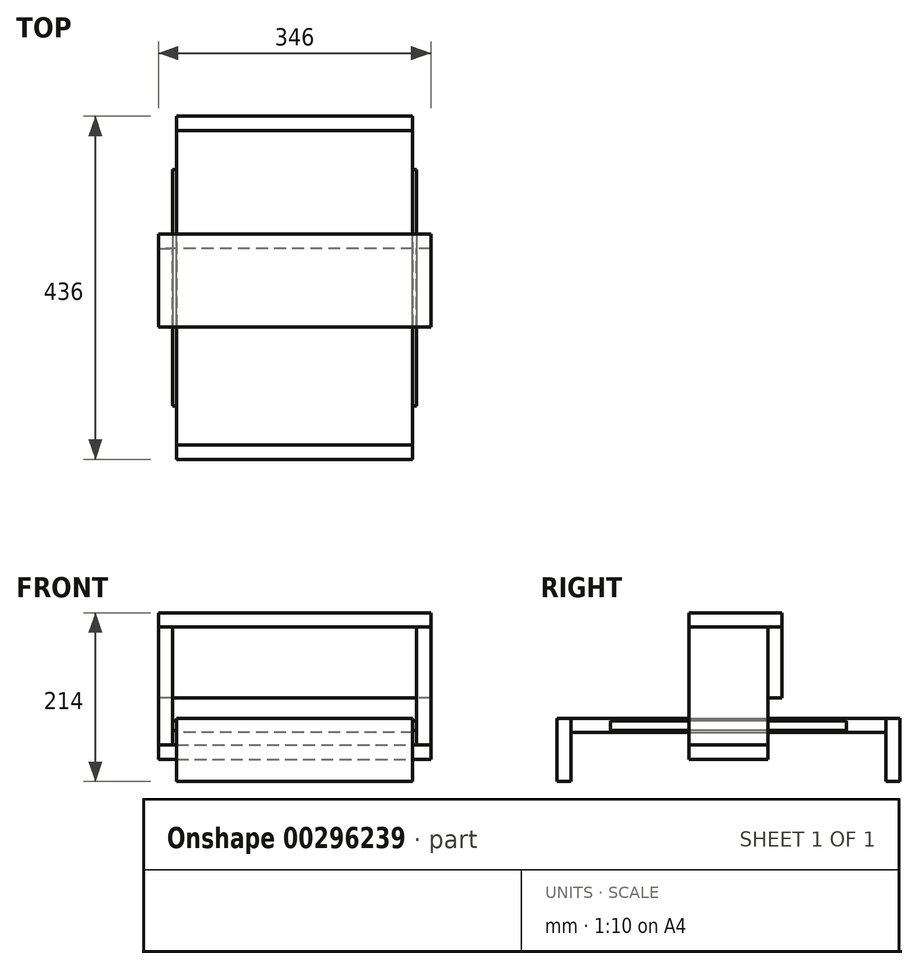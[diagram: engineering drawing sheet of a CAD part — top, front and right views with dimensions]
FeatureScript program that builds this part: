
annotation { "Feature Type Name" : "Feature", "Feature Type Description" : "" }
export const myFeature = defineFeature(function(context is Context, id is Id, definition is map)
    precondition{}
    {
        {
            var Q0;
            Q0=qCreatedBy(makeId("Front.planeOp"),FACE);
            var sketch = newSketch(context, id + "F0", { "sketchPlane" : qUnion([Q0])});
            skLineSegment(sketch, "E0.bottom", {"start": v(150, -9) * mm, "end": v(-150, -9) * mm});
            skLineSegment(sketch, "E0.top", {"start": v(150, 9) * mm, "end": v(-150, 9) * mm});
            skLineSegment(sketch, "E0.left", {"start": v(150, -9) * mm, "end": v(150, 9) * mm});
            skLineSegment(sketch, "E0.right", {"start": v(-150, -9) * mm, "end": v(-150, 9) * mm});
            skPoint(sketch, "E0.middle", {"position": v(0, 0) * mm});
            skSolve(sketch);
        }
        {
            var Q0;
            Q0=makeQuery(id+"F0.imprint","IMPRINT",FACE,{"disambiguationData":[TD([[makeQuery(id+"F0.imprint","IMPRINT",EDGE,{"derivedFrom":sQuery(id+"F0.wireOp",EDGE,"E0.bottom")}),-1.0]])]});
            extrude(context, id + "F1", {"entities" : qUnion([Q0]), "endBound" : BoundingType.SYMMETRIC, "depth" : 400 * mm});
        }
        {
            var Q0;
            Q0=makeQuery(id+"F1.opExtrude","SWEPT_FACE",FACE,{"disambiguationData":[OSD([sQuery(id+"F0.wireOp",EDGE,"E0.top")])]});
            var sketch = newSketch(context, id + "F2", { "sketchPlane" : qUnion([Q0])});
            skLineSegment(sketch, "E1.bottom", {"start": v(-150, -200) * mm, "end": v(150, -200) * mm});
            skLineSegment(sketch, "E1.top", {"start": v(-150, -218) * mm, "end": v(150, -218) * mm});
            skLineSegment(sketch, "E1.left", {"start": v(-150, -200) * mm, "end": v(-150, -218) * mm});
            skLineSegment(sketch, "E1.right", {"start": v(150, -200) * mm, "end": v(150, -218) * mm});
            skSolve(sketch);
        }
        {
            var Q0;
            Q0=makeQuery(id+"F2.imprint","IMPRINT",FACE,{"disambiguationData":[TD([[makeQuery(id+"F2.imprint","IMPRINT",EDGE,{"derivedFrom":sQuery(id+"F2.wireOp",EDGE,"E1.bottom")}),1.0]])]});
            extrude(context, id + "F3", {"entities" : qUnion([Q0]), "oppositeDirection" : true, "depth" : 80 * mm});
        }
        {
            var Q0;
            Q0=makeQuery(id+"F3.opExtrude","SWEPT_BODY",BODY,{"disambiguationData":[OSD([sQuery(id+"F2.wireOp",EDGE,"E1.bottom"),sQuery(id+"F2.wireOp",EDGE,"E1.top"),sQuery(id+"F2.wireOp",EDGE,"E1.left"),sQuery(id+"F2.wireOp",EDGE,"E1.right")])]});
            var Q1;
            Q1=qCreatedBy(makeId("Front.planeOp"),FACE);
            mirror(context, id + "F4", {"entities" : qUnion([Q0]), "mirrorPlane" : qUnion([Q1])});
        }
        {
            var Q0;
            Q0=makeQuery(id+"F1.opExtrude","SWEPT_FACE",FACE,{"disambiguationData":[OSD([sQuery(id+"F0.wireOp",EDGE,"E0.left")])]});
            var sketch = newSketch(context, id + "F5", { "sketchPlane" : qUnion([Q0])});
            skLineSegment(sketch, "E2.bottom", {"start": v(150, 6) * mm, "end": v(-150, 6) * mm});
            skLineSegment(sketch, "E2.top", {"start": v(150, -6) * mm, "end": v(-150, -6) * mm});
            skLineSegment(sketch, "E2.left", {"start": v(150, 6) * mm, "end": v(150, -6) * mm});
            skLineSegment(sketch, "E2.right", {"start": v(-150, 6) * mm, "end": v(-150, -6) * mm});
            skPoint(sketch, "E2.middle", {"position": v(0, 0) * mm});
            skSolve(sketch);
        }
        {
            var Q0;
            Q0=makeQuery(id+"F5.imprint","IMPRINT",FACE,{"disambiguationData":[TD([[makeQuery(id+"F5.imprint","IMPRINT",EDGE,{"derivedFrom":sQuery(id+"F5.wireOp",EDGE,"E2.bottom")}),1.0]])]});
            extrude(context, id + "F6", {"entities" : qUnion([Q0]), "depth" : 5 * mm});
        }
        {
            var Q0;
            Q0=makeQuery(id+"F6.opExtrude","SWEPT_BODY",BODY,{"disambiguationData":[OSD([sQuery(id+"F5.wireOp",EDGE,"E2.bottom"),sQuery(id+"F5.wireOp",EDGE,"E2.top"),sQuery(id+"F5.wireOp",EDGE,"E2.left"),sQuery(id+"F5.wireOp",EDGE,"E2.right")])]});
            var Q1;
            Q1=qCreatedBy(makeId("Right.planeOp"),FACE);
            mirror(context, id + "F7", {"entities" : qUnion([Q0]), "mirrorPlane" : qUnion([Q1])});
        }
        {
            var Q0;
            Q0=makeQuery(id+"F6.opExtrude","CAP_FACE",FACE,{"disambiguationData":[OSD([sQuery(id+"F5.wireOp",EDGE,"E2.bottom"),sQuery(id+"F5.wireOp",EDGE,"E2.top"),sQuery(id+"F5.wireOp",EDGE,"E2.left"),sQuery(id+"F5.wireOp",EDGE,"E2.right")])],"isStart":false});
            var sketch = newSketch(context, id + "F8", { "sketchPlane" : qUnion([Q0])});
            skLineSegment(sketch, "E3", {"start": v(0, 0) * mm, "end": v(0, -25) * mm});
            skLineSegment(sketch, "E4", {"start": v(0, -25) * mm, "end": v(50, -25) * mm});
            skLineSegment(sketch, "E5", {"start": v(50, -25) * mm, "end": v(50, 125) * mm});
            skLineSegment(sketch, "E6", {"start": v(50, 125) * mm, "end": v(-50, 125) * mm});
            skLineSegment(sketch, "E7", {"start": v(-50, 125) * mm, "end": v(-50, -25) * mm});
            skLineSegment(sketch, "E8", {"start": v(-50, -25) * mm, "end": v(0, -25) * mm});
            skSolve(sketch);
        }
        {
            var Q0;
            {var subQ0=sQuery(id+"F8.wireOp",EDGE,"E6");Q0=makeQuery(id+"F8.imprint","IMPRINT",FACE,{"disambiguationData":[TD([[makeQuery(id+"F8.imprint","IMPRINT",EDGE,{"derivedFrom":subQ0}),1.0]])]});}
            var Q1;
            {var subQ0=sQuery(id+"F8.wireOp",EDGE,"E8");Q1=makeQuery(id+"F8.imprint","IMPRINT",FACE,{"disambiguationData":[TD([[makeQuery(id+"F8.imprint","IMPRINT",EDGE,{"derivedFrom":subQ0}),1.0]])]});}
            var Q2;
            {var subQ0=sQuery(id+"F8.wireOp",EDGE,"E5");var subQ5=makeQuery(id+"F6.opExtrude","CAP_EDGE",EDGE,{"disambiguationData":[OSD([sQuery(id+"F5.wireOp",EDGE,"E2.top")])],"isStart":false});var subQ6=makeQuery(id+"F8.imprint","INTERSECT",VERTEX,{"derivedFrom":[subQ5,subQ0]});Q2=makeQuery(id+"F8.imprint","IMPRINT",FACE,{"disambiguationData":[TD([[makeQuery(id+"F8.imprint","IMPRINT",EDGE,{"disambiguationData":[TD([[subQ6,-1.0]])],"derivedFrom":subQ0}),1.0]])]});}
            var Q3;
            {var subQ0=sQuery(id+"F8.wireOp",EDGE,"E4");Q3=makeQuery(id+"F8.imprint","IMPRINT",FACE,{"disambiguationData":[TD([[makeQuery(id+"F8.imprint","IMPRINT",EDGE,{"derivedFrom":subQ0}),1.0]])]});}
            extrude(context, id + "F9", {"entities" : qUnion([Q0, Q1, Q2, Q3]), "depth" : 18 * mm});
        }
        {
            var Q0;
            Q0=makeQuery(id+"F9.opExtrude","SWEPT_BODY",BODY,{"disambiguationData":[OSD([sQuery(id+"F8.wireOp",EDGE,"E4"),sQuery(id+"F8.wireOp",EDGE,"E5"),sQuery(id+"F8.wireOp",EDGE,"E6"),sQuery(id+"F8.wireOp",EDGE,"E7"),sQuery(id+"F8.wireOp",EDGE,"E8")])]});
            var Q1;
            Q1=qCreatedBy(makeId("Right.planeOp"),FACE);
            mirror(context, id + "F10", {"entities" : qUnion([Q0]), "mirrorPlane" : qUnion([Q1])});
        }
        {
            var Q0;
            Q0=makeQuery(id+"F9.opExtrude","SWEPT_FACE",FACE,{"disambiguationData":[OSD([sQuery(id+"F8.wireOp",EDGE,"E4"),sQuery(id+"F8.wireOp",EDGE,"E8")])]});
            var sketch = newSketch(context, id + "F11", { "sketchPlane" : qUnion([Q0])});
            skPoint(sketch, "E9.0", {"position": v(-173, 50) * mm});
            skPoint(sketch, "E10.0", {"position": v(173, -50) * mm});
            skLineSegment(sketch, "E11.bottom", {"start": v(-173, 50) * mm, "end": v(173, 50) * mm});
            skLineSegment(sketch, "E11.top", {"start": v(-173, -50) * mm, "end": v(173, -50) * mm});
            skLineSegment(sketch, "E11.left", {"start": v(-173, 50) * mm, "end": v(-173, -50) * mm});
            skLineSegment(sketch, "E11.right", {"start": v(173, 50) * mm, "end": v(173, -50) * mm});
            skSolve(sketch);
        }
        {
            var Q0;
            {var subQ2=sQuery(id+"F11.wireOp",EDGE,"E11.left");Q0=makeQuery(id+"F11.imprint","IMPRINT",FACE,{"disambiguationData":[TD([[makeQuery(id+"F11.imprint","IMPRINT",EDGE,{"derivedFrom":subQ2}),1.0]])]});}
            var Q1;
            {var subQ2=sQuery(id+"F11.wireOp",EDGE,"E11.right");Q1=makeQuery(id+"F11.imprint","IMPRINT",FACE,{"disambiguationData":[TD([[makeQuery(id+"F11.imprint","IMPRINT",EDGE,{"derivedFrom":subQ2}),-1.0]])]});}
            extrude(context, id + "F12", {"entities" : qUnion([Q0, Q1]), "depth" : 18 * mm});
        }
        {
            var Q0;
            Q0=makeQuery(id+"F10.opPattern","COPY",FACE,{"derivedFrom":makeQuery(id+"F9.opExtrude","SWEPT_FACE",FACE,{"disambiguationData":[OSD([sQuery(id+"F8.wireOp",EDGE,"E5")])]}),"instanceName":"1"});
            var sketch = newSketch(context, id + "F13", { "sketchPlane" : qUnion([Q0])});
            skPoint(sketch, "E12.0", {"position": v(-173, 125) * mm});
            skPoint(sketch, "E13.0", {"position": v(173, 125) * mm});
            skLineSegment(sketch, "E14.bottom", {"start": v(-173, 125) * mm, "end": v(173, 125) * mm});
            skLineSegment(sketch, "E14.top", {"start": v(-173, 35) * mm, "end": v(173, 35) * mm});
            skLineSegment(sketch, "E14.left", {"start": v(-173, 125) * mm, "end": v(-173, 35) * mm});
            skLineSegment(sketch, "E14.right", {"start": v(173, 125) * mm, "end": v(173, 35) * mm});
            skSolve(sketch);
        }
        {
            var Q0;
            {var subQ3=sQuery(id+"F13.wireOp",EDGE,"E14.left");Q0=makeQuery(id+"F13.imprint","IMPRINT",FACE,{"disambiguationData":[TD([[makeQuery(id+"F13.imprint","IMPRINT",EDGE,{"derivedFrom":subQ3}),1.0]])]});}
            var Q1;
            {var subQ4=sQuery(id+"F13.wireOp",EDGE,"E14.right");Q1=makeQuery(id+"F13.imprint","IMPRINT",FACE,{"disambiguationData":[TD([[makeQuery(id+"F13.imprint","IMPRINT",EDGE,{"derivedFrom":subQ4}),1.0]])]});}
            extrude(context, id + "F14", {"entities" : qUnion([Q0, Q1]), "depth" : 18 * mm});
        }
        {
            var Q0;
            Q0=makeQuery(id+"F9.opExtrude","SWEPT_FACE",FACE,{"disambiguationData":[OSD([sQuery(id+"F8.wireOp",EDGE,"E6")])]});
            var sketch = newSketch(context, id + "F15", { "sketchPlane" : qUnion([Q0])});
            skPoint(sketch, "E15.0", {"position": v(-173, 68) * mm});
            skLineSegment(sketch, "E16.bottom", {"start": v(173, -50) * mm, "end": v(-173, -50) * mm});
            skLineSegment(sketch, "E16.top", {"start": v(173, 68) * mm, "end": v(-173, 68) * mm});
            skLineSegment(sketch, "E16.left", {"start": v(173, -50) * mm, "end": v(173, 68) * mm});
            skLineSegment(sketch, "E16.right", {"start": v(-173, -50) * mm, "end": v(-173, 68) * mm});
            skSolve(sketch);
        }
        {
            var Q0;
            {var subQ3=sQuery(id+"F15.wireOp",EDGE,"E16.top");Q0=makeQuery(id+"F15.imprint","IMPRINT",FACE,{"disambiguationData":[TD([[makeQuery(id+"F15.imprint","IMPRINT",EDGE,{"derivedFrom":subQ3}),1.0]])]});}
            var Q1;
            {var subQ1=sQuery(id+"F8.wireOp",EDGE,"E6");var subQ2=makeQuery(id+"F9.opExtrude","CAP_EDGE",EDGE,{"disambiguationData":[OSD([subQ1])],"isStart":true});Q1=makeQuery(id+"F15.imprint","IMPRINT",FACE,{"disambiguationData":[TD([[makeQuery(id+"F15.imprint","IMPRINT",EDGE,{"derivedFrom":subQ2}),1.0]])]});}
            extrude(context, id + "F16", {"entities" : qUnion([Q0, Q1]), "depth" : 18 * mm});
        }
    });
